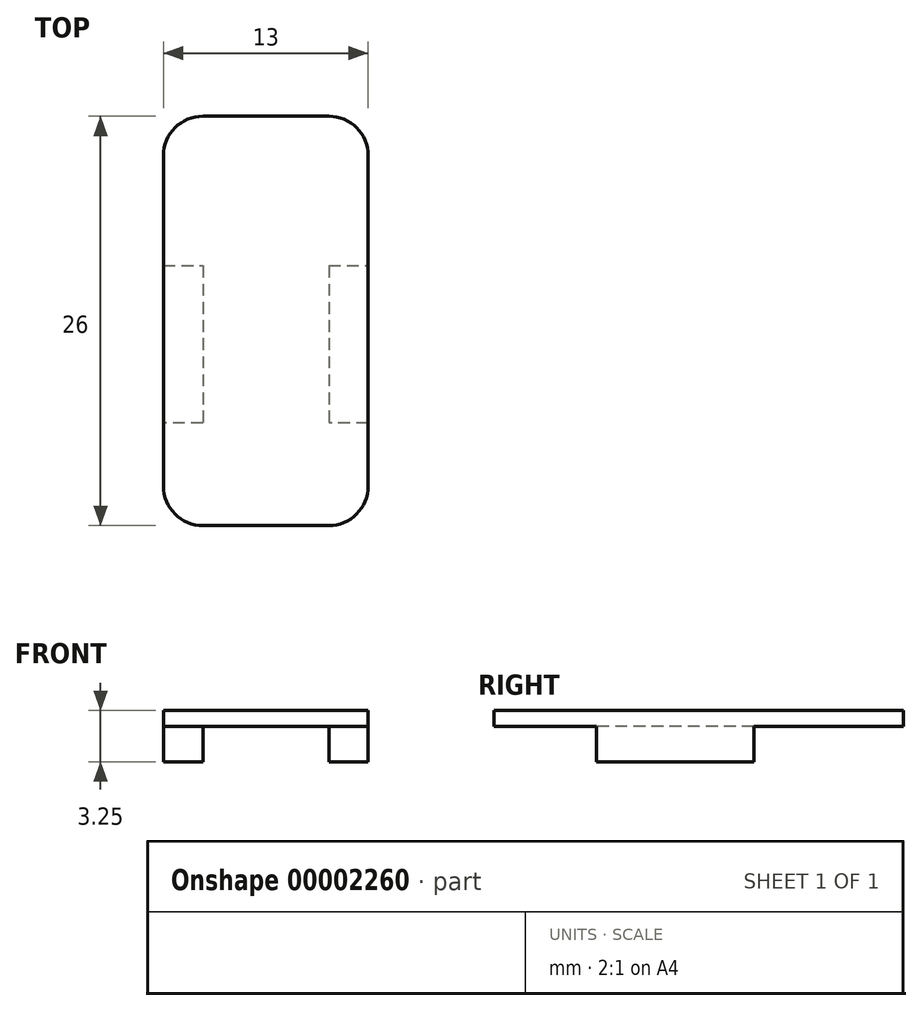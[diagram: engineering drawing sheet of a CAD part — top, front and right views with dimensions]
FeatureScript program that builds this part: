
annotation { "Feature Type Name" : "Feature", "Feature Type Description" : "" }
export const myFeature = defineFeature(function(context is Context, id is Id, definition is map)
    precondition{}
    {
        {
            var Q0;
            Q0=qCreatedBy(makeId("Top.planeOp"),FACE);
            var sketch = newSketch(context, id + "F0", { "sketchPlane" : qUnion([Q0])});
            skLineSegment(sketch, "E0.bottom", {"start": v(0, 0) * mm, "end": v(13, 0) * mm});
            skLineSegment(sketch, "E0.top", {"start": v(0, -26) * mm, "end": v(13, -26) * mm});
            skLineSegment(sketch, "E0.left", {"start": v(0, 0) * mm, "end": v(0, -26) * mm});
            skLineSegment(sketch, "E0.right", {"start": v(13, 0) * mm, "end": v(13, -26) * mm});
            skLineSegment(sketch, "E1", {"start": v(10.5, 0) * mm, "end": v(10.5, -26) * mm});
            skLineSegment(sketch, "E2", {"start": v(2.5, 0) * mm, "end": v(2.5, -26) * mm});
            skLineSegment(sketch, "E3", {"start": v(0, -9.5) * mm, "end": v(13, -9.5) * mm});
            skLineSegment(sketch, "E4", {"start": v(13, -19.5) * mm, "end": v(0, -19.5) * mm});
            skSolve(sketch);
        }
        {
            var Q0;
            {var subQ0=sQuery(id+"F0.wireOp",EDGE,"E0.left");var subQ1=sQuery(id+"F0.wireOp",EDGE,"E0.bottom");var subQ2=makeQuery(id+"F0.imprint","INTERSECT",VERTEX,{"derivedFrom":[subQ1,subQ0]});Q0=makeQuery(id+"F0.imprint","IMPRINT",FACE,{"disambiguationData":[TD([[makeQuery(id+"F0.imprint","IMPRINT",EDGE,{"disambiguationData":[TD([[subQ2,-1.0]])],"derivedFrom":subQ1}),-1.0]])]});}
            var Q1;
            {var subQ0=sQuery(id+"F0.wireOp",EDGE,"E3");var subQ1=sQuery(id+"F0.wireOp",EDGE,"E0.left");var subQ2=makeQuery(id+"F0.imprint","INTERSECT",VERTEX,{"derivedFrom":[subQ1,subQ0]});Q1=makeQuery(id+"F0.imprint","IMPRINT",FACE,{"disambiguationData":[TD([[makeQuery(id+"F0.imprint","IMPRINT",EDGE,{"disambiguationData":[TD([[subQ2,-1.0]])],"derivedFrom":subQ1}),1.0]])]});}
            var Q2;
            {var subQ0=sQuery(id+"F0.wireOp",EDGE,"E0.left");var subQ1=sQuery(id+"F0.wireOp",EDGE,"E0.top");var subQ2=makeQuery(id+"F0.imprint","INTERSECT",VERTEX,{"derivedFrom":[subQ1,subQ0]});Q2=makeQuery(id+"F0.imprint","IMPRINT",FACE,{"disambiguationData":[TD([[makeQuery(id+"F0.imprint","IMPRINT",EDGE,{"disambiguationData":[TD([[subQ2,-1.0]])],"derivedFrom":subQ1}),1.0]])]});}
            var Q3;
            {var subQ0=sQuery(id+"F0.wireOp",EDGE,"E1");var subQ1=sQuery(id+"F0.wireOp",EDGE,"E0.top");var subQ2=makeQuery(id+"F0.imprint","INTERSECT",VERTEX,{"derivedFrom":[subQ1,subQ0]});Q3=makeQuery(id+"F0.imprint","IMPRINT",FACE,{"disambiguationData":[TD([[makeQuery(id+"F0.imprint","IMPRINT",EDGE,{"disambiguationData":[TD([[subQ2,1.0]])],"derivedFrom":subQ1}),1.0]])]});}
            var Q4;
            {var subQ0=sQuery(id+"F0.wireOp",EDGE,"E0.right");var subQ1=sQuery(id+"F0.wireOp",EDGE,"E0.top");var subQ2=makeQuery(id+"F0.imprint","INTERSECT",VERTEX,{"derivedFrom":[subQ1,subQ0]});Q4=makeQuery(id+"F0.imprint","IMPRINT",FACE,{"disambiguationData":[TD([[makeQuery(id+"F0.imprint","IMPRINT",EDGE,{"disambiguationData":[TD([[subQ2,1.0]])],"derivedFrom":subQ1}),1.0]])]});}
            var Q5;
            {var subQ0=sQuery(id+"F0.wireOp",EDGE,"E3");var subQ1=sQuery(id+"F0.wireOp",EDGE,"E0.right");var subQ2=makeQuery(id+"F0.imprint","INTERSECT",VERTEX,{"derivedFrom":[subQ1,subQ0]});Q5=makeQuery(id+"F0.imprint","IMPRINT",FACE,{"disambiguationData":[TD([[makeQuery(id+"F0.imprint","IMPRINT",EDGE,{"disambiguationData":[TD([[subQ2,-1.0]])],"derivedFrom":subQ1}),-1.0]])]});}
            var Q6;
            {var subQ0=sQuery(id+"F0.wireOp",EDGE,"E0.right");var subQ1=sQuery(id+"F0.wireOp",EDGE,"E0.bottom");var subQ2=makeQuery(id+"F0.imprint","INTERSECT",VERTEX,{"derivedFrom":[subQ1,subQ0]});Q6=makeQuery(id+"F0.imprint","IMPRINT",FACE,{"disambiguationData":[TD([[makeQuery(id+"F0.imprint","IMPRINT",EDGE,{"disambiguationData":[TD([[subQ2,1.0]])],"derivedFrom":subQ1}),-1.0]])]});}
            var Q7;
            {var subQ0=sQuery(id+"F0.wireOp",EDGE,"E1");var subQ1=sQuery(id+"F0.wireOp",EDGE,"E0.bottom");var subQ2=makeQuery(id+"F0.imprint","INTERSECT",VERTEX,{"derivedFrom":[subQ1,subQ0]});Q7=makeQuery(id+"F0.imprint","IMPRINT",FACE,{"disambiguationData":[TD([[makeQuery(id+"F0.imprint","IMPRINT",EDGE,{"disambiguationData":[TD([[subQ2,1.0]])],"derivedFrom":subQ1}),-1.0]])]});}
            var Q8;
            {var subQ0=sQuery(id+"F0.wireOp",EDGE,"E3");var subQ1=sQuery(id+"F0.wireOp",EDGE,"E1");var subQ2=makeQuery(id+"F0.imprint","INTERSECT",VERTEX,{"derivedFrom":[subQ1,subQ0]});Q8=makeQuery(id+"F0.imprint","IMPRINT",FACE,{"disambiguationData":[TD([[makeQuery(id+"F0.imprint","IMPRINT",EDGE,{"disambiguationData":[TD([[subQ2,-1.0]])],"derivedFrom":subQ1}),-1.0]])]});}
            extrude(context, id + "F1", {"entities" : qUnion([Q0, Q1, Q2, Q3, Q4, Q5, Q6, Q7, Q8]), "depth" : 1 * mm});
        }
        {
            var Q0;
            {var subQ0=sQuery(id+"F0.wireOp",EDGE,"E3");var subQ1=sQuery(id+"F0.wireOp",EDGE,"E0.right");var subQ2=makeQuery(id+"F0.imprint","INTERSECT",VERTEX,{"derivedFrom":[subQ1,subQ0]});Q0=makeQuery(id+"F0.imprint","IMPRINT",FACE,{"disambiguationData":[TD([[makeQuery(id+"F0.imprint","IMPRINT",EDGE,{"disambiguationData":[TD([[subQ2,-1.0]])],"derivedFrom":subQ1}),-1.0]])]});}
            var Q1;
            {var subQ0=sQuery(id+"F0.wireOp",EDGE,"E3");var subQ1=sQuery(id+"F0.wireOp",EDGE,"E0.left");var subQ2=makeQuery(id+"F0.imprint","INTERSECT",VERTEX,{"derivedFrom":[subQ1,subQ0]});Q1=makeQuery(id+"F0.imprint","IMPRINT",FACE,{"disambiguationData":[TD([[makeQuery(id+"F0.imprint","IMPRINT",EDGE,{"disambiguationData":[TD([[subQ2,-1.0]])],"derivedFrom":subQ1}),1.0]])]});}
            extrude(context, id + "F2", {"entities" : qUnion([Q0, Q1]), "operationType" : NewBodyOperationType.ADD, "oppositeDirection" : true, "depth" : 2.25 * mm});
        }
        {
            var Q0;
            Q0=makeQuery(id+"F1.opExtrude","SWEPT_EDGE",EDGE,{"disambiguationData":[OSD([sQuery(id+"F0.wireOp",EDGE,"E0.top"),sQuery(id+"F0.wireOp",EDGE,"E0.right")])]});
            var Q1;
            Q1=makeQuery(id+"F1.opExtrude","SWEPT_EDGE",EDGE,{"disambiguationData":[OSD([sQuery(id+"F0.wireOp",EDGE,"E0.bottom"),sQuery(id+"F0.wireOp",EDGE,"E0.right")])]});
            var Q2;
            Q2=makeQuery(id+"F1.opExtrude","SWEPT_EDGE",EDGE,{"disambiguationData":[OSD([sQuery(id+"F0.wireOp",EDGE,"E0.bottom"),sQuery(id+"F0.wireOp",EDGE,"E0.left")])]});
            var Q3;
            Q3=makeQuery(id+"F1.opExtrude","SWEPT_EDGE",EDGE,{"disambiguationData":[OSD([sQuery(id+"F0.wireOp",EDGE,"E0.top"),sQuery(id+"F0.wireOp",EDGE,"E0.left")])]});
            fillet(context, id + "F3", {"entities" : qUnion([Q0, Q1, Q2, Q3]), "radius" : 2.5 * mm, "tangentPropagation" : true, "allowEdgeOverflow" : false});
        }
    });
